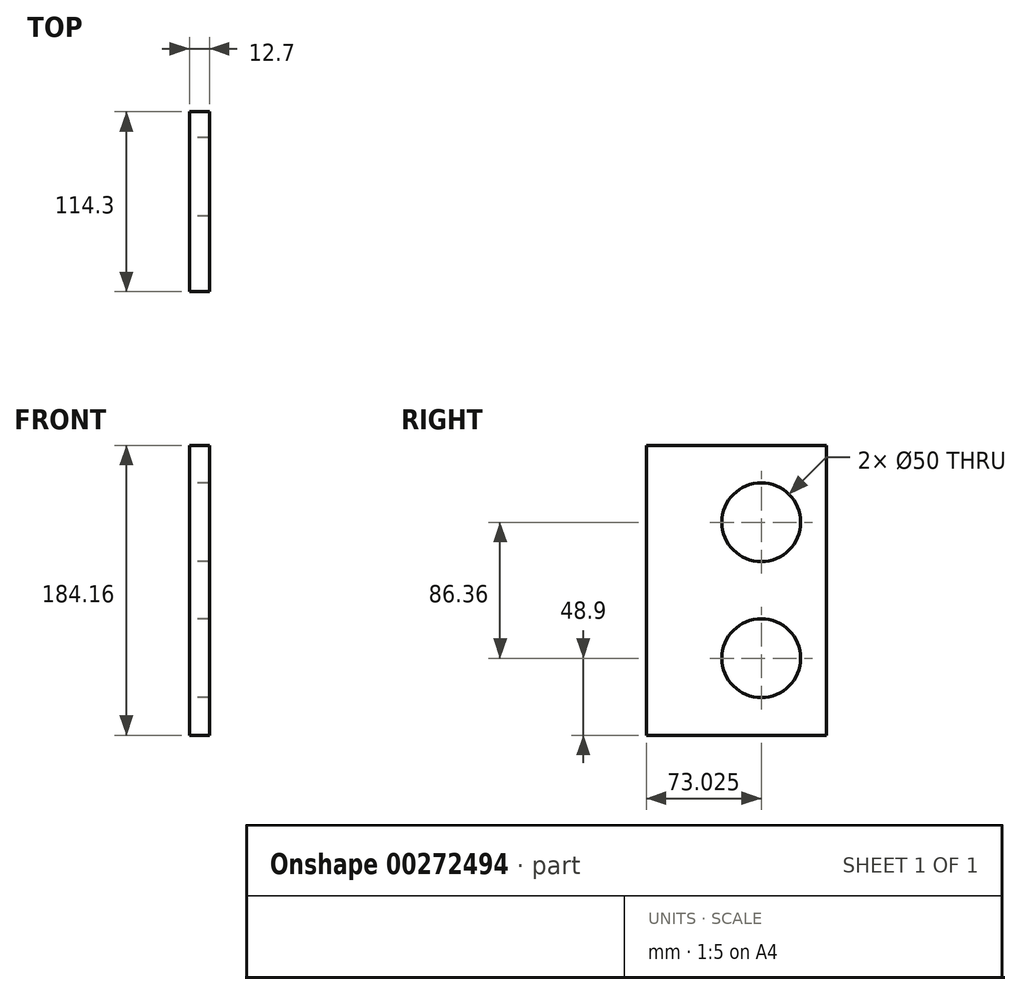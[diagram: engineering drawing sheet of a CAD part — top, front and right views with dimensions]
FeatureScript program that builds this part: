
annotation { "Feature Type Name" : "Feature", "Feature Type Description" : "" }
export const myFeature = defineFeature(function(context is Context, id is Id, definition is map)
    precondition{}
    {
        {
            var Q0;
            Q0=qCreatedBy(makeId("Right.planeOp"),FACE);
            var sketch = newSketch(context, id + "F0", { "sketchPlane" : qUnion([Q0])});
            skLineSegment(sketch, "E0.bottom", {"start": v(-57.15, 92.08) * mm, "end": v(57.15, 92.08) * mm});
            skLineSegment(sketch, "E0.top", {"start": v(-57.15, -92.08) * mm, "end": v(57.15, -92.08) * mm});
            skLineSegment(sketch, "E0.left", {"start": v(-57.15, 92.07) * mm, "end": v(-57.15, -92.07) * mm});
            skLineSegment(sketch, "E0.right", {"start": v(57.15, 92.08) * mm, "end": v(57.15, -92.07) * mm});
            skPoint(sketch, "E0.middle", {"position": v(0, 0) * mm});
            skCircle(sketch, "E1", {"center": v(15.88, -43.18) * mm, "radius": 25 * mm});
            skCircle(sketch, "E2", {"center": v(15.88, 43.18) * mm, "radius": 25 * mm});
            skLineSegment(sketch, "E3", {"start": v(0, 0) * mm, "end": v(15.88, 0) * mm});
            skLineSegment(sketch, "E4", {"start": v(15.88, 0) * mm, "end": v(15.88, 43.18) * mm});
            skLineSegment(sketch, "E5", {"start": v(15.88, 43.18) * mm, "end": v(15.88, -43.18) * mm});
            skSolve(sketch);
        }
        {
            var Q0;
            Q0 = qSketchRegion(id + "F0", true);
            extrude(context, id + "F1", {"entities" : qUnion([Q0]), "endBound" : BoundingType.SYMMETRIC, "depth" : 12.7 * mm, "offsetDistance" : 25.4 * mm});
        }
    });
